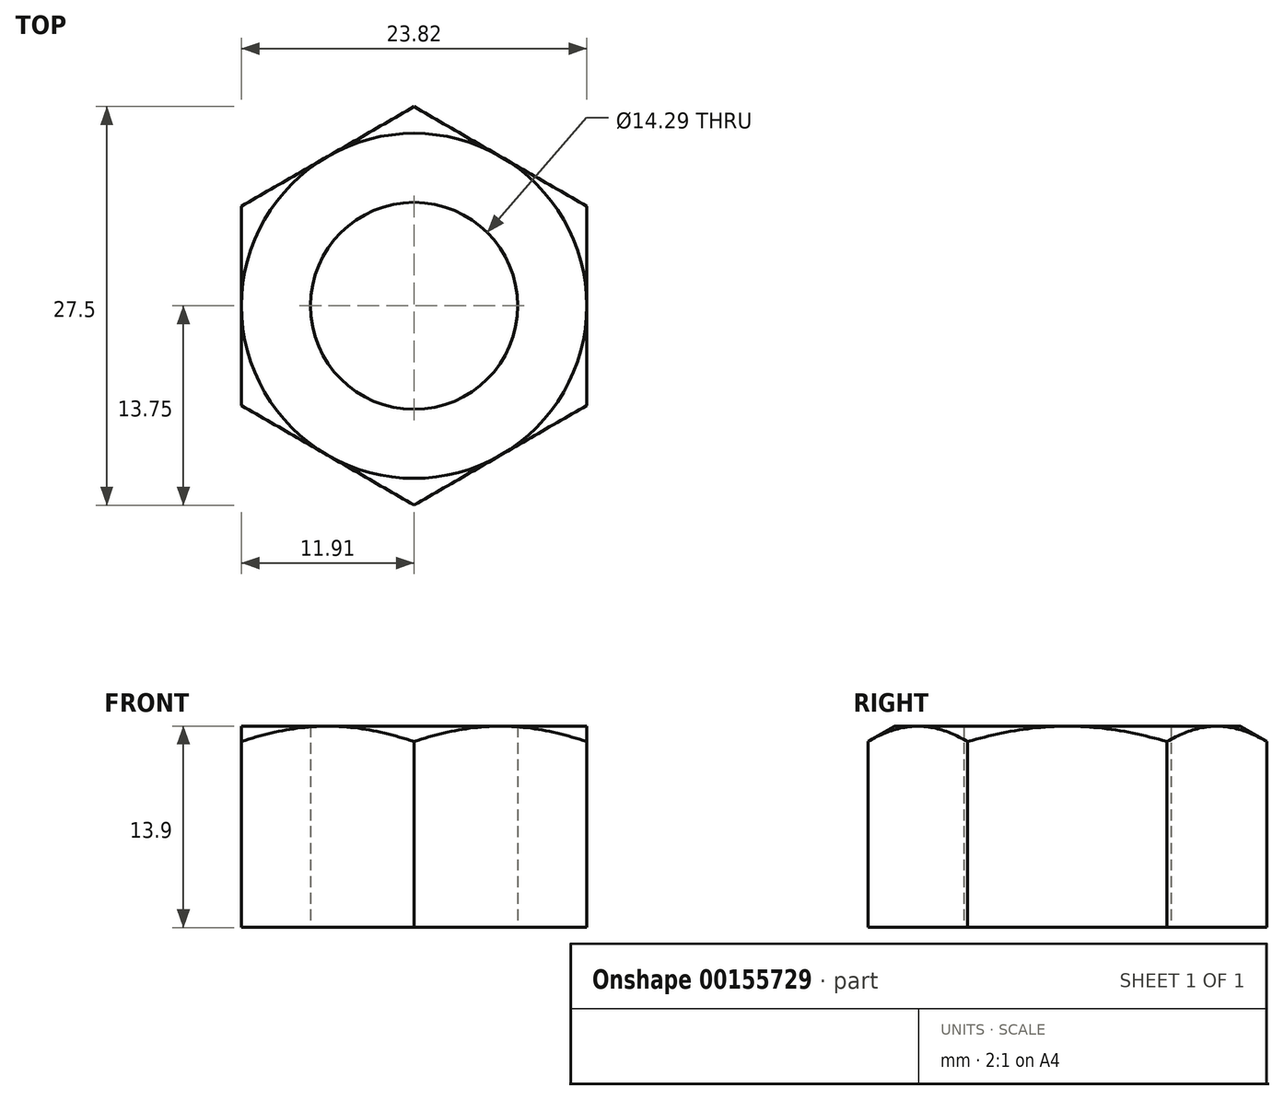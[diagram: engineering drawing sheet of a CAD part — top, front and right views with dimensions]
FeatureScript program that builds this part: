
annotation { "Feature Type Name" : "Feature", "Feature Type Description" : "" }
export const myFeature = defineFeature(function(context is Context, id is Id, definition is map)
    precondition{}
    {
        {
            var Q0;
            Q0=qCreatedBy(makeId("Top.planeOp"),FACE);
            var sketch = newSketch(context, id + "F0", { "sketchPlane" : qUnion([Q0])});
            skCircle(sketch, "E0.cCircle", {"center": v(0, 0) * mm, "radius": 11.9 * mm, "construction": true});
            skLineSegment(sketch, "E0.0", {"start": v(11.9, 6.87) * mm, "end": v(11.9, -6.87) * mm});
            skLineSegment(sketch, "E0.1", {"start": v(11.9, -6.87) * mm, "end": v(0, -13.75) * mm});
            skLineSegment(sketch, "E0.2", {"start": v(0, -13.75) * mm, "end": v(-11.9, -6.87) * mm});
            skLineSegment(sketch, "E0.3", {"start": v(-11.9, -6.87) * mm, "end": v(-11.9, 6.87) * mm});
            skLineSegment(sketch, "E0.4", {"start": v(-11.9, 6.87) * mm, "end": v(0, 13.75) * mm});
            skLineSegment(sketch, "E0.5", {"start": v(0, 13.75) * mm, "end": v(11.9, 6.87) * mm});
            skPoint(sketch, "E0.0.midPoint", {"position": v(11.9, 0) * mm});
            skCircle(sketch, "E1", {"center": v(0, 0) * mm, "radius": 7.14 * mm});
            skSolve(sketch);
        }
        {
            var Q0;
            Q0 = qSketchRegion(id + "F0", true);
            extrude(context, id + "F1", {"entities" : qUnion([Q0]), "endBound" : BoundingType.SYMMETRIC, "depth" : 13.9 * mm});
        }
        {
            var Q0;
            Q0=qCreatedBy(makeId("Front.planeOp"),FACE);
            var sketch = newSketch(context, id + "F2", { "sketchPlane" : qUnion([Q0])});
            skLineSegment(sketch, "E2", {"start": v(11.9, 6.95) * mm, "end": v(15.57, 6.95) * mm});
            skLineSegment(sketch, "E3", {"start": v(15.57, 6.95) * mm, "end": v(15.57, 4.83) * mm});
            skLineSegment(sketch, "E4", {"start": v(15.57, 4.83) * mm, "end": v(11.9, 6.95) * mm});
            skLineSegment(sketch, "E5", {"start": v(0, 0) * mm, "end": v(0, 16.08) * mm, "construction": true});
            skSolve(sketch);
        }
        {
            var Q0;
            Q0 = qSketchRegion(id + "F2", true);
            var Q1;
            Q1=sQuery(id+"F2.wireOp",EDGE,"E5");
            revolve(context, id + "F3", {"operationType" : NewBodyOperationType.REMOVE, "entities" : qUnion([Q0]), "axis" : qUnion([Q1]), "revolveType" : RevolveType.FULL, "oppositeDirection" : true});
        }
    });
